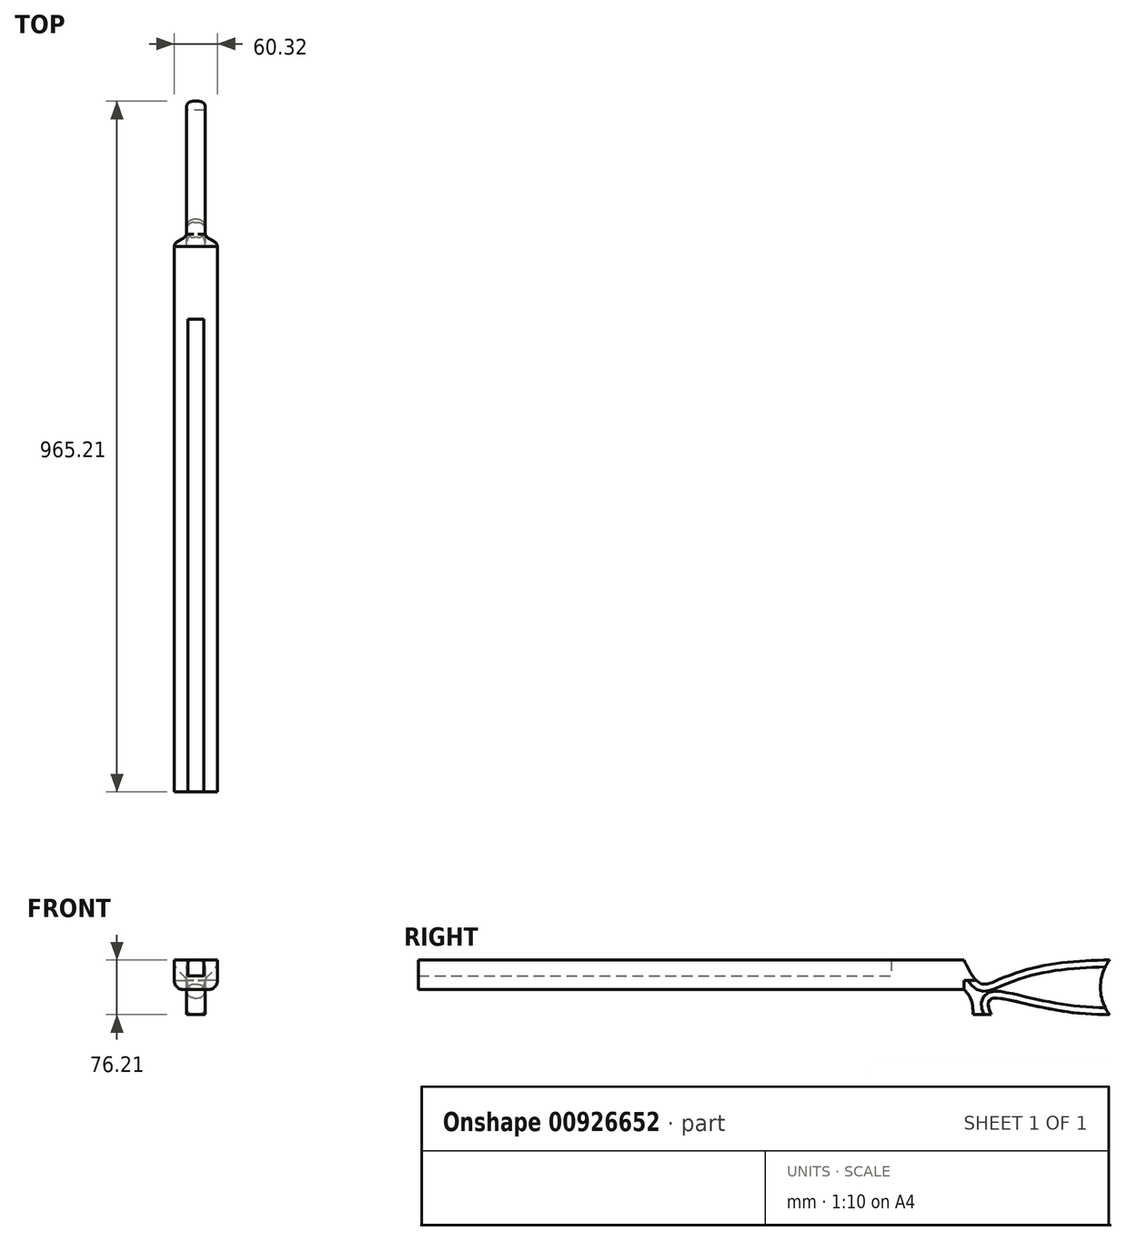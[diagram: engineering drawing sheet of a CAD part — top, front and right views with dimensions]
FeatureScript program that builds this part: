
annotation { "Feature Type Name" : "Feature", "Feature Type Description" : "" }
export const myFeature = defineFeature(function(context is Context, id is Id, definition is map)
    precondition{}
    {
        {
            var Q0;
            Q0=qCreatedBy(makeId("Front.planeOp"),FACE);
            var sketch = newSketch(context, id + "F0", { "sketchPlane" : qUnion([Q0])});
            skLineSegment(sketch, "E0.bottom", {"start": v(17.46, 0) * mm, "end": v(-17.46, 0) * mm});
            skLineSegment(sketch, "E0.top", {"start": v(30.16, 41.28) * mm, "end": v(11.11, 41.27) * mm});
            skLineSegment(sketch, "E0.left", {"start": v(30.16, 12.7) * mm, "end": v(30.16, 41.28) * mm});
            skLineSegment(sketch, "E0.right", {"start": v(-30.16, 12.7) * mm, "end": v(-30.16, 41.27) * mm});
            skPoint(sketch, "E0.middle", {"position": v(0, 20.64) * mm});
            skLineSegment(sketch, "E1.top", {"start": v(11.11, 19.05) * mm, "end": v(-11.11, 19.05) * mm});
            skLineSegment(sketch, "E1.left", {"start": v(11.11, 41.27) * mm, "end": v(11.11, 19.05) * mm});
            skLineSegment(sketch, "E1.right", {"start": v(-11.11, 41.27) * mm, "end": v(-11.11, 19.05) * mm});
            skPoint(sketch, "E1.middle", {"position": v(0, 30.16) * mm});
            skLineSegment(sketch, "E2.trimOffspring", {"start": v(-11.11, 41.27) * mm, "end": v(-30.16, 41.27) * mm});
            skPoint(sketch, "E3.visualSharp", {"position": v(30.16, 0) * mm});
            skArc(sketch, "E3.filletArc", {"start": v(17.46, 0) * mm, "mid": v(26.44, 3.72) * mm, "end": v(30.16, 12.7) * mm});
            skPoint(sketch, "E4.visualSharp", {"position": v(-30.16, 0) * mm});
            skArc(sketch, "E4.filletArc", {"start": v(-30.16, 12.7) * mm, "mid": v(-26.44, 3.72) * mm, "end": v(-17.46, 0) * mm});
            skPoint(sketch, "E5.visualSharp", {"position": v(11.11, 19.05) * mm});
            skLineSegment(sketch, "E5.filletArc", {"start": v(11.11, 19.05) * mm, "end": v(11.11, 19.05) * mm});
            skPoint(sketch, "E6.visualSharp", {"position": v(-11.11, 19.05) * mm});
            skLineSegment(sketch, "E6.filletArc", {"start": v(-11.11, 19.05) * mm, "end": v(-11.11, 19.05) * mm});
            skSolve(sketch);
        }
        {
            var Q0;
            Q0=makeQuery(id+"F0.imprint","IMPRINT",FACE,{"disambiguationData":[TD([[makeQuery(id+"F0.imprint","IMPRINT",EDGE,{"derivedFrom":sQuery(id+"F0.wireOp",EDGE,"E0.bottom")}),-1.0]])]});
            extrude(context, id + "F1", {"entities" : qUnion([Q0]), "depth" : 381 * mm, "offsetDistance" : 25.4 * mm, "hasSecondDirection" : true, "secondDirectionOppositeDirection" : true, "secondDirectionDepth" : 381 * mm});
        }
        {
            var Q0;
            Q0=qCreatedBy(makeId("Right.planeOp"),FACE);
            var sketch = newSketch(context, id + "F2", { "sketchPlane" : qUnion([Q0])});
            skLineSegment(sketch, "E7.bottom", {"start": v(381, 41.28) * mm, "end": v(584.2, 41.28) * mm});
            skLineSegment(sketch, "E7.top", {"start": v(393.7, -34.92) * mm, "end": v(419.1, -34.92) * mm});
            skLineSegment(sketch, "E7.left", {"start": v(381, 41.28) * mm, "end": v(381, 0) * mm});
            skLineSegment(sketch, "E7.right", {"start": v(584.2, 41.28) * mm, "end": v(584.2, -34.92) * mm, "construction": true});
            skArc(sketch, "E8", {"start": v(584.2, 41.28) * mm, "mid": v(571.5, 3.18) * mm, "end": v(584.2, -34.92) * mm});
            skFitSpline(sketch, "E9", {"points": [v(381, 41.28) * mm, v(584.2, 41.28) * mm], "startDerivative": vector(114.3, -228.6) * mm, "endDerivative": vector(561.98, 0) * mm});
            skFitSpline(sketch, "E10", {"points": [v(584.2, -34.92) * mm, v(434.98, -12.7) * mm, v(419.1, -34.92) * mm], "startDerivative": vector(-298.7, 0) * mm, "endDerivative": vector(111.7, -255.3) * mm});
            skFitSpline(sketch, "E11", {"points": [v(393.7, -34.93) * mm, v(381, 0) * mm], "startDerivative": vector(0, 57.15) * mm, "endDerivative": vector(-28.58, 28.58) * mm});
            skPoint(sketch, "E12.orphan", {"position": v(381, -34.92) * mm});
            skSolve(sketch);
        }
        {
            var Q0;
            Q0 = qSketchRegion(id + "F2", true);
            extrude(context, id + "F3", {"entities" : qUnion([Q0]), "operationType" : NewBodyOperationType.ADD, "depth" : 12.7 * mm, "offsetDistance" : 25.4 * mm, "hasSecondDirection" : true, "secondDirectionOppositeDirection" : true, "secondDirectionDepth" : 12.7 * mm});
        }
        {
            var Q0;
            Q0=qCreatedBy(makeId("Top.planeOp"),FACE);
            var sketch = newSketch(context, id + "F4", { "sketchPlane" : qUnion([Q0])});
            skLineSegment(sketch, "E13.bottom", {"start": v(30.16, 381) * mm, "end": v(12.7, 381) * mm});
            skLineSegment(sketch, "E13.top", {"start": v(30.16, 400.05) * mm, "end": v(12.7, 400.05) * mm, "construction": true});
            skLineSegment(sketch, "E13.left", {"start": v(30.16, 381) * mm, "end": v(30.16, 400.05) * mm, "construction": true});
            skLineSegment(sketch, "E13.right", {"start": v(12.7, 381) * mm, "end": v(12.7, 400.05) * mm});
            skFitSpline(sketch, "E14", {"points": [v(30.16, 381) * mm, v(12.7, 400.05) * mm], "startDerivative": vector(0, 28.58) * mm, "endDerivative": vector(0, 28.58) * mm});
            skLineSegment(sketch, "E15", {"start": v(0, 400.05) * mm, "end": v(0, 381) * mm, "construction": true});
            skLineSegment(sketch, "E16.MirrorCS", {"start": v(-12.7, 381) * mm, "end": v(-12.7, 400.05) * mm});
            skLineSegment(sketch, "E17.MirrorCS", {"start": v(-30.16, 381) * mm, "end": v(-12.7, 381) * mm});
            skFitSpline(sketch, "E18.MirrorCS", {"points": [v(-30.16, 381) * mm, v(-12.7, 400.05) * mm], "startDerivative": vector(0, 28.58) * mm, "endDerivative": vector(0, 28.58) * mm});
            skSolve(sketch);
        }
        {
            var Q0;
            Q0=makeQuery(id+"F4.imprint","IMPRINT",FACE,{"disambiguationData":[TD([[makeQuery(id+"F4.imprint","IMPRINT",EDGE,{"derivedFrom":sQuery(id+"F4.wireOp",EDGE,"E16.MirrorCS")}),1.0]])]});
            var Q1;
            Q1=makeQuery(id+"F4.imprint","IMPRINT",FACE,{"disambiguationData":[TD([[makeQuery(id+"F4.imprint","IMPRINT",EDGE,{"derivedFrom":sQuery(id+"F4.wireOp",EDGE,"E13.bottom")}),-1.0]])]});
            extrude(context, id + "F5", {"entities" : qUnion([Q0, Q1]), "operationType" : NewBodyOperationType.ADD, "depth" : 41.27 * mm, "offsetDistance" : 25.4 * mm, "hasSecondDirection" : true, "secondDirectionOppositeDirection" : false, "secondDirectionDepth" : 12.7 * mm});
        }
        {
            var Q0;
            Q0=makeQuery(id+"F2.imprint","IMPRINT",FACE,{"disambiguationData":[TD([[makeQuery(id+"F2.imprint","IMPRINT",EDGE,{"derivedFrom":sQuery(id+"F2.wireOp",EDGE,"E7.bottom")}),-1.0]])]});
            extrude(context, id + "F6", {"entities" : qUnion([Q0]), "operationType" : NewBodyOperationType.REMOVE, "oppositeDirection" : true, "depth" : 38.1 * mm, "offsetDistance" : 25.4 * mm, "hasSecondDirection" : true, "secondDirectionOppositeDirection" : false, "secondDirectionDepth" : 38.1 * mm});
        }
        {
            var Q0;
            Q0=makeQuery(id+"F6.boolean.opBoolean","INTERSECT",EDGE,{"derivedFrom":[makeQuery(id+"F3.opExtrude","CAP_FACE",FACE,{"disambiguationData":[OSD([sQuery(id+"F2.wireOp",EDGE,"E7.bottom"),sQuery(id+"F2.wireOp",EDGE,"E7.top"),sQuery(id+"F2.wireOp",EDGE,"E7.left"),sQuery(id+"F2.wireOp",EDGE,"E8"),sQuery(id+"F2.wireOp",EDGE,"E10"),sQuery(id+"F2.wireOp",EDGE,"E11")])],"isStart":false}),makeQuery(id+"F6.opExtrude","SWEPT_FACE",FACE,{"disambiguationData":[OSD([sQuery(id+"F2.wireOp",EDGE,"E9")])]})]});
            var Q1;
            Q1=makeQuery(id+"F3.opExtrude","CAP_EDGE",EDGE,{"disambiguationData":[OSD([sQuery(id+"F2.wireOp",EDGE,"E11")])],"isStart":false});
            var Q2;
            Q2=makeQuery(id+"F3.opExtrude","CAP_EDGE",EDGE,{"disambiguationData":[OSD([sQuery(id+"F2.wireOp",EDGE,"E10")])],"isStart":false});
            var Q3;
            Q3=makeQuery(id+"F3.opExtrude","CAP_EDGE",EDGE,{"disambiguationData":[OSD([sQuery(id+"F2.wireOp",EDGE,"E11")])],"isStart":true});
            var Q4;
            Q4=makeQuery(id+"F3.opExtrude","CAP_EDGE",EDGE,{"disambiguationData":[OSD([sQuery(id+"F2.wireOp",EDGE,"E10")])],"isStart":true});
            var Q5;
            Q5=makeQuery(id+"F6.boolean.opBoolean","INTERSECT",EDGE,{"derivedFrom":[makeQuery(id+"F3.opExtrude","CAP_FACE",FACE,{"disambiguationData":[OSD([sQuery(id+"F2.wireOp",EDGE,"E7.bottom"),sQuery(id+"F2.wireOp",EDGE,"E7.top"),sQuery(id+"F2.wireOp",EDGE,"E7.left"),sQuery(id+"F2.wireOp",EDGE,"E8"),sQuery(id+"F2.wireOp",EDGE,"E10"),sQuery(id+"F2.wireOp",EDGE,"E11")])],"isStart":true}),makeQuery(id+"F6.opExtrude","SWEPT_FACE",FACE,{"disambiguationData":[OSD([sQuery(id+"F2.wireOp",EDGE,"E9")])]})]});
            fillet(context, id + "F7", {"entities" : qUnion([Q0, Q1, Q2, Q3, Q4, Q5]), "radius" : 9.52 * mm, "allowEdgeOverflow" : false});
        }
        {
            var Q0;
            Q0=qCreatedBy(makeId("Top.planeOp"),FACE);
            var sketch = newSketch(context, id + "F8", { "sketchPlane" : qUnion([Q0])});
            skLineSegment(sketch, "E19.bottom", {"start": v(11.11, 279.4) * mm, "end": v(-11.11, 279.4) * mm});
            skLineSegment(sketch, "E19.top", {"start": v(11.11, 381) * mm, "end": v(-11.11, 381) * mm});
            skLineSegment(sketch, "E19.left", {"start": v(11.11, 279.4) * mm, "end": v(11.11, 381) * mm});
            skLineSegment(sketch, "E19.right", {"start": v(-11.11, 279.4) * mm, "end": v(-11.11, 381) * mm});
            skPoint(sketch, "E19.middle", {"position": v(0, 330.2) * mm});
            skSolve(sketch);
        }
        {
            var Q0;
            Q0 = qSketchRegion(id + "F8", true);
            extrude(context, id + "F9", {"entities" : qUnion([Q0]), "operationType" : NewBodyOperationType.ADD, "depth" : 41.27 * mm, "offsetDistance" : 25.4 * mm});
        }
    });
